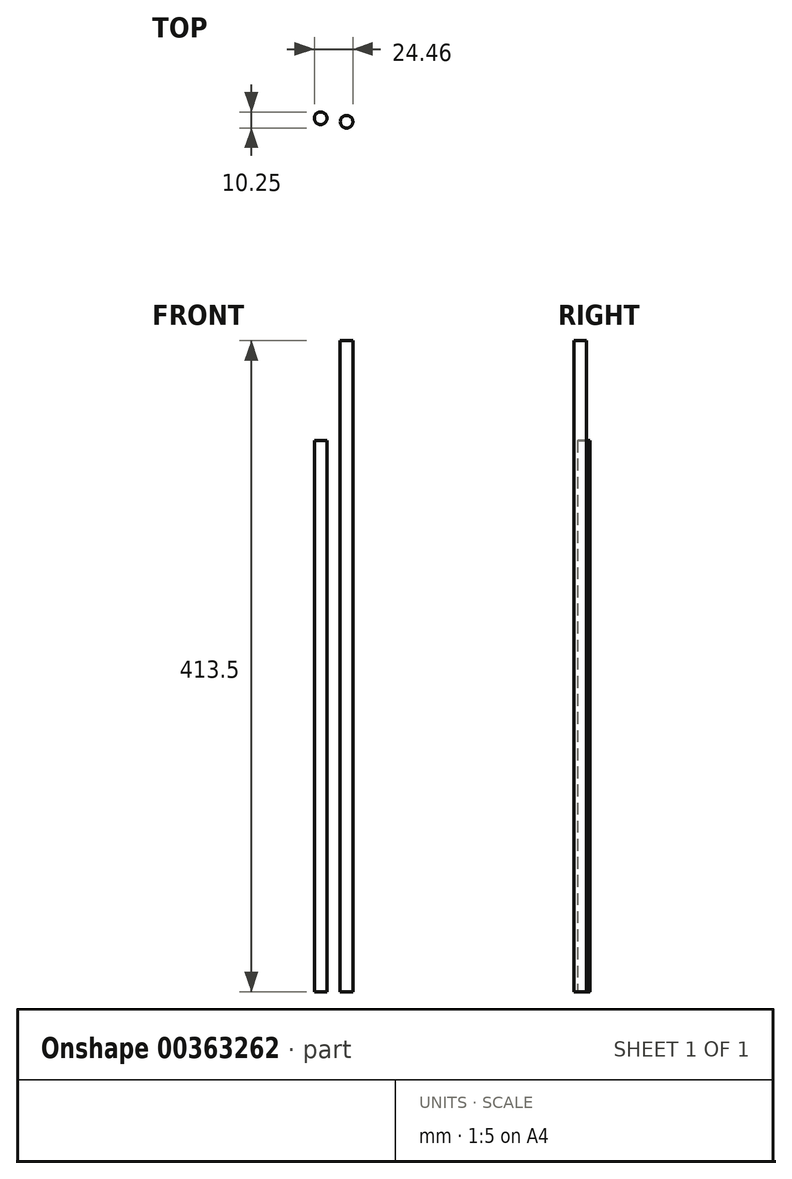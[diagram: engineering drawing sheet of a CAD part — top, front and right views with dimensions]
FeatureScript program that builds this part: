
annotation { "Feature Type Name" : "Feature", "Feature Type Description" : "" }
export const myFeature = defineFeature(function(context is Context, id is Id, definition is map)
    precondition{}
    {
        {
            var Q0;
            Q0=qCreatedBy(makeId("Top.planeOp"),FACE);
            var sketch = newSketch(context, id + "F0", { "sketchPlane" : qUnion([Q0])});
            skCircle(sketch, "E0", {"center": v(0, 0) * mm, "radius": 4 * mm});
            skCircle(sketch, "E1", {"center": v(16.46, -2.25) * mm, "radius": 4 * mm});
            skSolve(sketch);
        }
        {
            var Q0;
            Q0=makeQuery(id+"F0.imprint","IMPRINT",FACE,{"disambiguationData":[TD([[makeQuery(id+"F0.imprint","IMPRINT",EDGE,{"derivedFrom":sQuery(id+"F0.wireOp",EDGE,"E0")}),1.0]])]});
            extrude(context, id + "F1", {"entities" : qUnion([Q0]), "depth" : 350 * mm});
        }
        {
            var Q0;
            Q0=makeQuery(id+"F0.imprint","IMPRINT",FACE,{"disambiguationData":[TD([[makeQuery(id+"F0.imprint","IMPRINT",EDGE,{"derivedFrom":sQuery(id+"F0.wireOp",EDGE,"E1")}),1.0]])]});
            var Q1;
            Q1=sQuery(id+"F0.wireOp",EDGE,"E1");
            extrude(context, id + "F2", {"entities" : qUnion([Q0]), "surfaceEntities" : qUnion([Q1]), "depth" : 413.5 * mm});
        }
    });
